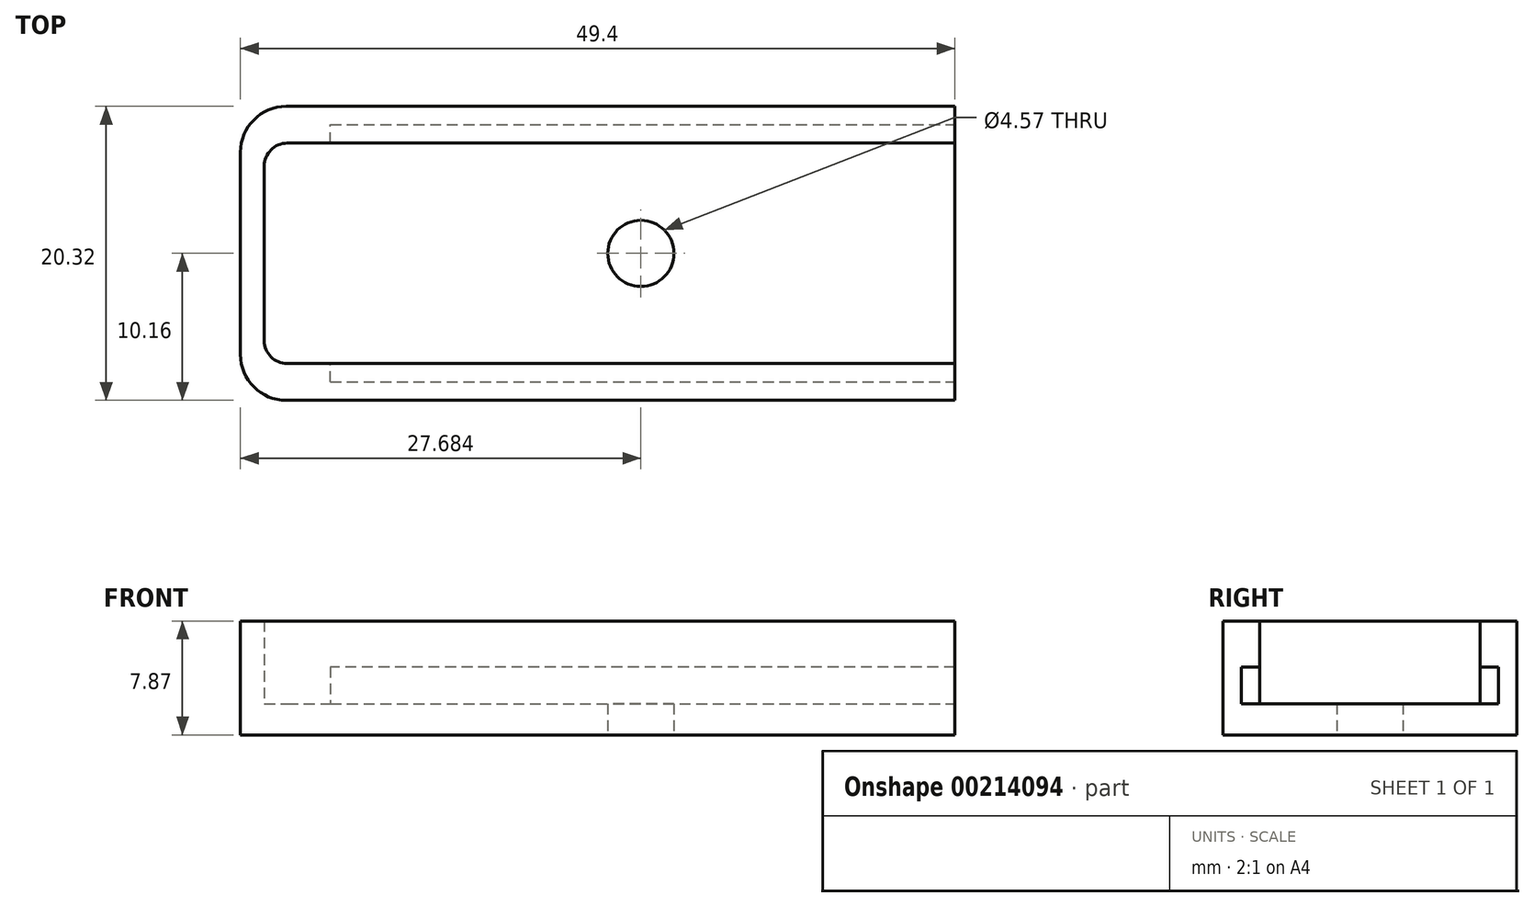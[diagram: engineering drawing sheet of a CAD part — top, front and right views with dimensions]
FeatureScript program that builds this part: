
annotation { "Feature Type Name" : "Feature", "Feature Type Description" : "" }
export const myFeature = defineFeature(function(context is Context, id is Id, definition is map)
    precondition{}
    {
        {
            var Q0;
            Q0=qCreatedBy(makeId("Top.planeOp"),FACE);
            var sketch = newSketch(context, id + "F0", { "sketchPlane" : qUnion([Q0]), "disableImprinting" : false});
            skLineSegment(sketch, "E0.bottom", {"start": v(-21.53, -10.16) * mm, "end": v(24.7, -10.16) * mm});
            skLineSegment(sketch, "E0.top", {"start": v(-21.53, 10.16) * mm, "end": v(24.7, 10.16) * mm});
            skLineSegment(sketch, "E0.left", {"start": v(-24.7, -6.99) * mm, "end": v(-24.7, 6.99) * mm});
            skLineSegment(sketch, "E0.right", {"start": v(24.7, -10.16) * mm, "end": v(24.7, 10.16) * mm});
            skPoint(sketch, "E0.middle", {"position": v(0, 0) * mm});
            skPoint(sketch, "E1.visualSharp", {"position": v(-24.7, 10.16) * mm});
            skArc(sketch, "E1.filletArc", {"start": v(-21.53, 10.16) * mm, "mid": v(-23.77, 9.23) * mm, "end": v(-24.7, 6.99) * mm});
            skPoint(sketch, "E2.visualSharp", {"position": v(-24.7, -10.16) * mm});
            skArc(sketch, "E2.filletArc", {"start": v(-24.7, -6.99) * mm, "mid": v(-23.77, -9.23) * mm, "end": v(-21.53, -10.16) * mm});
            skLineSegment(sketch, "E3.bottom", {"start": v(-21.46, 7.62) * mm, "end": v(24.7, 7.62) * mm});
            skLineSegment(sketch, "E3.top", {"start": v(-21.46, -7.62) * mm, "end": v(24.7, -7.62) * mm});
            skLineSegment(sketch, "E3.left", {"start": v(-23.05, 6.03) * mm, "end": v(-23.05, -6.03) * mm});
            skLineSegment(sketch, "E3.right", {"start": v(24.7, 7.62) * mm, "end": v(24.7, -7.62) * mm});
            skPoint(sketch, "E4.visualSharp", {"position": v(-23.05, 7.62) * mm});
            skArc(sketch, "E4.filletArc", {"start": v(-21.46, 7.62) * mm, "mid": v(-22.59, 7.16) * mm, "end": v(-23.05, 6.03) * mm});
            skPoint(sketch, "E5.visualSharp", {"position": v(-23.05, -7.62) * mm});
            skArc(sketch, "E5.filletArc", {"start": v(-23.05, -6.03) * mm, "mid": v(-22.59, -7.16) * mm, "end": v(-21.46, -7.62) * mm});
            skCircle(sketch, "E6", {"center": v(2.98, 0) * mm, "radius": 2.29 * mm});
            skSolve(sketch);
        }
        {
            var Q0;
            Q0=makeQuery(id+"F0.imprint","IMPRINT",FACE,{"disambiguationData":[TD([[makeQuery(id+"F0.imprint","IMPRINT",EDGE,{"derivedFrom":sQuery(id+"F0.wireOp",EDGE,"E0.bottom")}),1.0]])]});
            extrude(context, id + "F1", {"entities" : qUnion([Q0]), "depth" : 7.87 * mm});
        }
        {
            var Q0;
            Q0=makeQuery(id+"F0.imprint","IMPRINT",FACE,{"disambiguationData":[TD([[makeQuery(id+"F0.imprint","IMPRINT",EDGE,{"derivedFrom":sQuery(id+"F0.wireOp",EDGE,"E3.bottom")}),-1.0]])]});
            extrude(context, id + "F2", {"entities" : qUnion([Q0]), "operationType" : NewBodyOperationType.ADD, "depth" : 2.16 * mm});
        }
        {
            var Q0;
            {var subQ0=sQuery(id+"F0.wireOp",EDGE,"E3.right");var subQ1=sQuery(id+"F0.wireOp",EDGE,"E0.right");Q0=makeQuery(id+"F2.boolean.opBoolean","MERGE",FACE,{"derivedFrom":[makeQuery(id+"F1.opExtrude","SWEPT_FACE",FACE,{"disambiguationData":[OSD([subQ1]),TDD([makeQuery(id+"F0.imprint","IMPRINT",EDGE,{"disambiguationData":[TD([[makeQuery(id+"F0.imprint","INTERSECT",VERTEX,{"derivedFrom":[sQuery(id+"F0.wireOp",EDGE,"E0.bottom"),subQ1]}),-1.0]])],"derivedFrom":subQ1})])]}),makeQuery(id+"F1.opExtrude","SWEPT_FACE",FACE,{"disambiguationData":[OSD([subQ1]),TDD([makeQuery(id+"F0.imprint","IMPRINT",EDGE,{"disambiguationData":[TD([[makeQuery(id+"F0.imprint","INTERSECT",VERTEX,{"derivedFrom":[sQuery(id+"F0.wireOp",EDGE,"E0.top"),subQ1]}),1.0]])],"derivedFrom":subQ1})])]}),makeQuery(id+"F2.opExtrude","SWEPT_FACE",FACE,{"disambiguationData":[OSD([subQ0])]})]});}
            var sketch = newSketch(context, id + "F3", { "sketchPlane" : qUnion([Q0])});
            skLineSegment(sketch, "E7.bottom", {"start": v(-8.89, 4.7) * mm, "end": v(8.9, 4.7) * mm});
            skLineSegment(sketch, "E7.left", {"start": v(-8.89, 4.7) * mm, "end": v(-8.89, 2.16) * mm});
            skLineSegment(sketch, "E7.right", {"start": v(8.9, 4.7) * mm, "end": v(8.9, 2.16) * mm});
            skPoint(sketch, "E7.middle", {"position": v(0, 2.16) * mm});
            skLineSegment(sketch, "E8", {"start": v(-8.89, 2.16) * mm, "end": v(8.9, 2.16) * mm});
            skPoint(sketch, "E7.top.start.orphan", {"position": v(-8.89, -0.38) * mm});
            skPoint(sketch, "E9.orphan", {"position": v(8.9, -0.38) * mm});
            skSolve(sketch);
        }
        {
            var Q0;
            Q0 = qSketchRegion(id + "F3", true);
            extrude(context, id + "F4", {"entities" : qUnion([Q0]), "operationType" : NewBodyOperationType.REMOVE, "oppositeDirection" : true, "depth" : 43.18 * mm});
        }
    });
